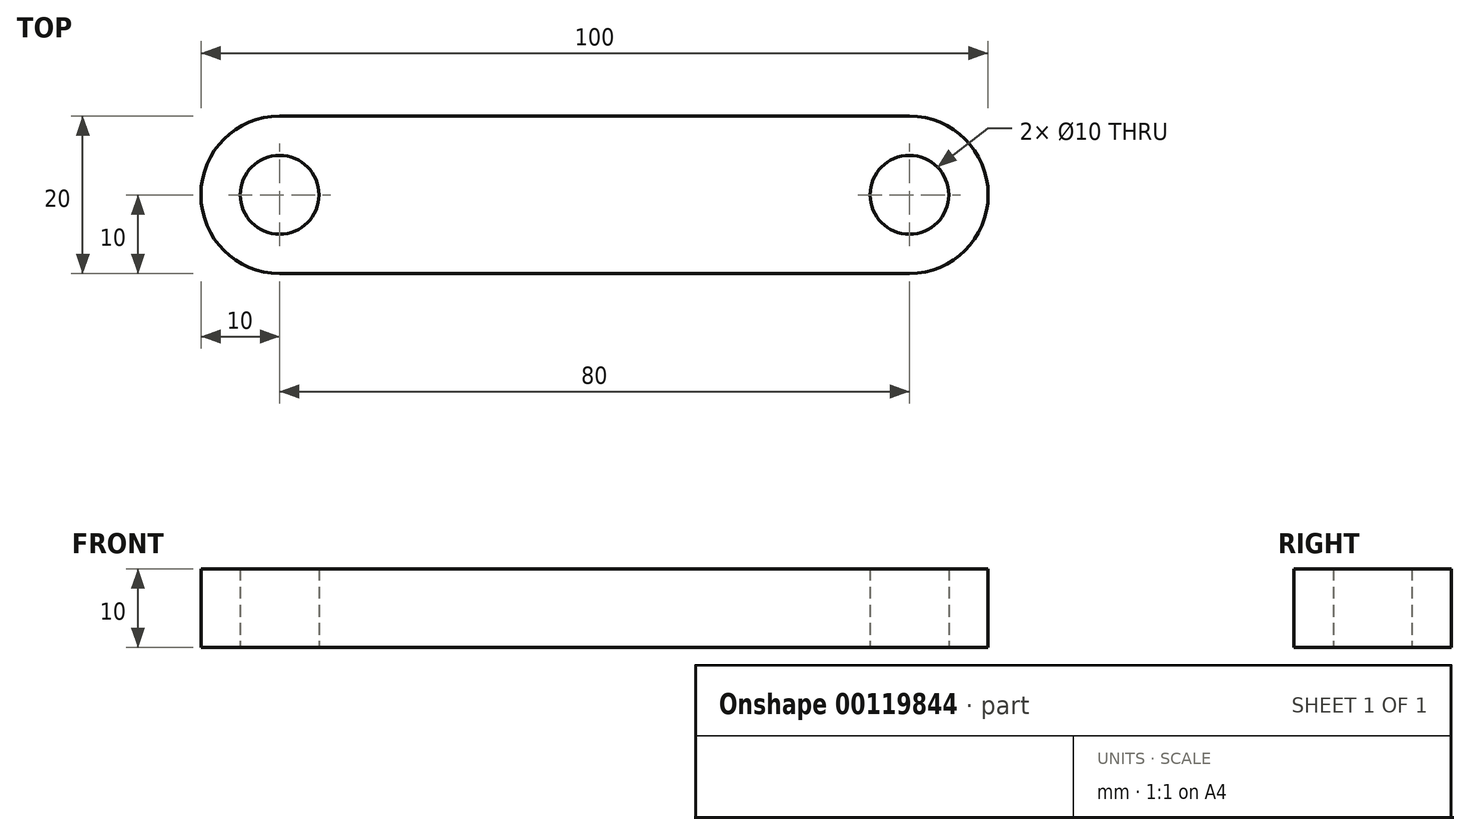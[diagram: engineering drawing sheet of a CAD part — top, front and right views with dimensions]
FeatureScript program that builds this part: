
annotation { "Feature Type Name" : "Feature", "Feature Type Description" : "" }
export const myFeature = defineFeature(function(context is Context, id is Id, definition is map)
    precondition{}
    {
        {
            var Q0;
            Q0=qCreatedBy(makeId("Top.planeOp"),FACE);
            var sketch = newSketch(context, id + "F0", { "sketchPlane" : qUnion([Q0])});
            skLineSegment(sketch, "E0", {"start": v(0, 20) * mm, "end": v(80, 20) * mm});
            skLineSegment(sketch, "E1", {"start": v(0, 0) * mm, "end": v(80, 0) * mm});
            skArc(sketch, "E2", {"start": v(0, 20) * mm, "mid": v(-10, 10) * mm, "end": v(0, 0) * mm});
            skPoint(sketch, "E3", {"position": v(-10, 10) * mm});
            skArc(sketch, "E4", {"start": v(80, 0) * mm, "mid": v(90, 10) * mm, "end": v(80, 20) * mm});
            skLineSegment(sketch, "E5", {"start": v(-36.77, 10) * mm, "end": v(104.17, 10) * mm, "construction": true});
            skCircle(sketch, "E6", {"center": v(0, 10) * mm, "radius": 5 * mm});
            skCircle(sketch, "E7", {"center": v(80, 10) * mm, "radius": 5 * mm});
            skSolve(sketch);
        }
        {
            var Q0;
            Q0=makeQuery(id+"F0.imprint","IMPRINT",FACE,{"disambiguationData":[TD([[makeQuery(id+"F0.imprint","IMPRINT",EDGE,{"derivedFrom":sQuery(id+"F0.wireOp",EDGE,"E0")}),-1.0]])]});
            extrude(context, id + "F1", {"entities" : qUnion([Q0]), "depth" : 10 * mm});
        }
    });
